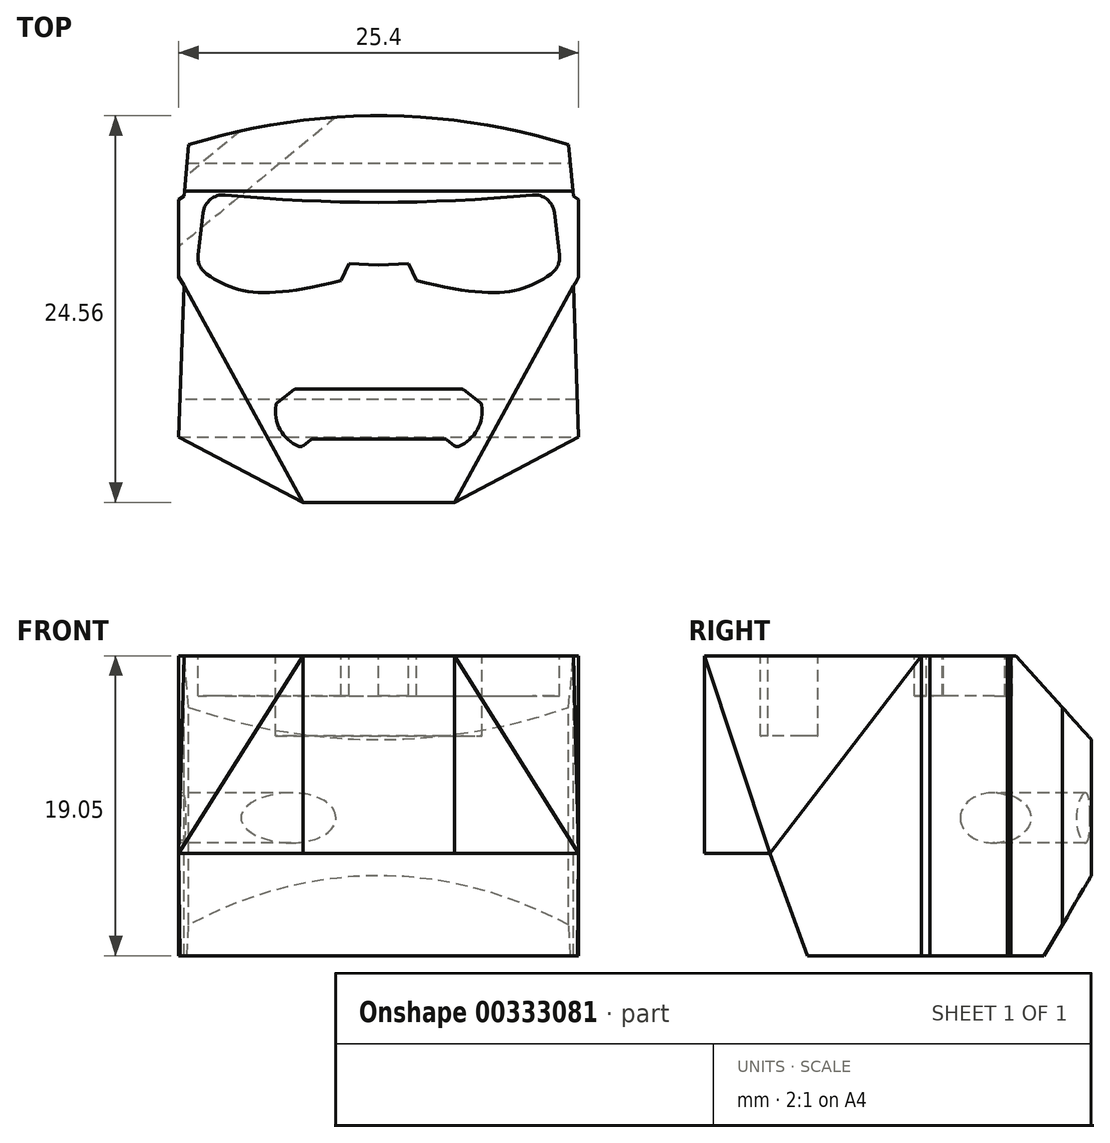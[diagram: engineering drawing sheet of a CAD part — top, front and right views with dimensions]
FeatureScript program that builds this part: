
annotation { "Feature Type Name" : "Feature", "Feature Type Description" : "" }
export const myFeature = defineFeature(function(context is Context, id is Id, definition is map)
    precondition{}
    {
        {
            var Q0;
            Q0=qCreatedBy(makeId("Top.planeOp"),FACE);
            var sketch = newSketch(context, id + "F0", { "sketchPlane" : qUnion([Q0])});
            skLineSegment(sketch, "E0.bottom", {"start": v(-12.7, 12.7) * mm, "end": v(12.7, 12.7) * mm});
            skLineSegment(sketch, "E0.top", {"start": v(-12.7, -12.7) * mm, "end": v(12.7, -12.7) * mm});
            skLineSegment(sketch, "E0.left", {"start": v(-12.7, 12.7) * mm, "end": v(-12.7, -12.7) * mm});
            skLineSegment(sketch, "E0.right", {"start": v(12.7, 12.7) * mm, "end": v(12.7, -12.7) * mm});
            skPoint(sketch, "E0.middle", {"position": v(0, 0) * mm});
            skSolve(sketch);
        }
        {
            var Q0;
            Q0 = qSketchRegion(id + "F0", true);
            extrude(context, id + "F1", {"entities" : qUnion([Q0]), "depth" : 19.05 * mm});
        }
        {
            var Q0;
            Q0=makeQuery(id+"F1.opExtrude","CAP_FACE",FACE,{"disambiguationData":[OSD([sQuery(id+"F0.wireOp",EDGE,"E0.bottom"),sQuery(id+"F0.wireOp",EDGE,"E0.top"),sQuery(id+"F0.wireOp",EDGE,"E0.left"),sQuery(id+"F0.wireOp",EDGE,"E0.right")])],"isStart":false});
            var sketch = newSketch(context, id + "F2", { "sketchPlane" : qUnion([Q0])});
            skLineSegment(sketch, "E1", {"start": v(-12.07, 10.02) * mm, "end": v(12.07, 10.02) * mm, "construction": true});
            skArc(sketch, "E2", {"start": v(12.06, 10.02) * mm, "mid": v(0, 11.86) * mm, "end": v(-12.07, 10.02) * mm});
            skLineSegment(sketch, "E3", {"start": v(-12.07, 10.02) * mm, "end": v(-12.38, 6.75) * mm});
            skLineSegment(sketch, "E4", {"start": v(-12.38, 6.75) * mm, "end": v(-12.7, 6.54) * mm});
            skLineSegment(sketch, "E5", {"start": v(-12.7, 6.54) * mm, "end": v(-12.7, 1.62) * mm});
            skLineSegment(sketch, "E6", {"start": v(-12.7, 1.62) * mm, "end": v(-12.38, 1.07) * mm});
            skLineSegment(sketch, "E7", {"start": v(-12.38, 1.07) * mm, "end": v(-12.7, -8.54) * mm});
            skLineSegment(sketch, "E8", {"start": v(-12.7, -8.54) * mm, "end": v(-4.82, -12.7) * mm});
            skLineSegment(sketch, "E9", {"start": v(-4.82, -12.7) * mm, "end": v(0, -12.7) * mm});
            skLineSegment(sketch, "E10.MirrorCS", {"start": v(4.82, -12.7) * mm, "end": v(0, -12.7) * mm});
            skLineSegment(sketch, "E11.MirrorCS", {"start": v(12.07, 10.02) * mm, "end": v(12.38, 6.75) * mm});
            skLineSegment(sketch, "E12.MirrorCS", {"start": v(12.7, 1.62) * mm, "end": v(12.38, 1.07) * mm});
            skLineSegment(sketch, "E13.MirrorCS", {"start": v(12.38, 6.75) * mm, "end": v(12.7, 6.54) * mm});
            skLineSegment(sketch, "E14.MirrorCS", {"start": v(12.38, 1.07) * mm, "end": v(12.7, -8.54) * mm});
            skLineSegment(sketch, "E15.MirrorCS", {"start": v(12.7, 6.54) * mm, "end": v(12.7, 1.62) * mm});
            skLineSegment(sketch, "E16.MirrorCS", {"start": v(12.7, -8.54) * mm, "end": v(4.82, -12.7) * mm});
            skLineSegment(sketch, "E17.bottom", {"start": v(15.39, 14.33) * mm, "end": v(-17.73, 14.33) * mm});
            skLineSegment(sketch, "E17.top", {"start": v(15.39, -14.33) * mm, "end": v(-17.73, -14.33) * mm});
            skLineSegment(sketch, "E17.left", {"start": v(15.39, 14.33) * mm, "end": v(15.39, -14.33) * mm});
            skLineSegment(sketch, "E17.right", {"start": v(-17.73, 14.33) * mm, "end": v(-17.73, -14.33) * mm});
            skPoint(sketch, "E17.middle", {"position": v(-1.17, 0) * mm});
            skSolve(sketch);
        }
        {
            var Q0;
            Q0 = qSketchRegion(id + "F2", true);
            extrude(context, id + "F3", {"entities" : qUnion([Q0]), "operationType" : NewBodyOperationType.REMOVE, "endBound" : BoundingType.THROUGH_ALL, "oppositeDirection" : true, "depth" : 25.4 * mm});
        }
        {
            var Q0;
            Q0=qCreatedBy(makeId("Right.planeOp"),FACE);
            var sketch = newSketch(context, id + "F4", { "sketchPlane" : qUnion([Q0])});
            skLineSegment(sketch, "E18", {"start": v(6.62, 19.56) * mm, "end": v(12.73, 12.77) * mm});
            skLineSegment(sketch, "E19", {"start": v(12.73, 12.77) * mm, "end": v(13.43, 23.23) * mm});
            skLineSegment(sketch, "E20", {"start": v(13.43, 23.23) * mm, "end": v(6.62, 19.56) * mm});
            skSolve(sketch);
        }
        {
            var Q0;
            Q0 = qSketchRegion(id + "F4", true);
            extrude(context, id + "F5", {"entities" : qUnion([Q0]), "operationType" : NewBodyOperationType.REMOVE, "endBound" : BoundingType.SYMMETRIC, "oppositeDirection" : true, "depth" : 25.4 * mm});
        }
        {
            var Q0;
            Q0=makeQuery(id+"F1.opExtrude","CAP_FACE",FACE,{"disambiguationData":[OSD([sQuery(id+"F0.wireOp",EDGE,"E0.bottom"),sQuery(id+"F0.wireOp",EDGE,"E0.top"),sQuery(id+"F0.wireOp",EDGE,"E0.left"),sQuery(id+"F0.wireOp",EDGE,"E0.right")])],"isStart":false});
            var sketch = newSketch(context, id + "F6", { "sketchPlane" : qUnion([Q0])});
            skLineSegment(sketch, "E21", {"start": v(-12.07, 7.08) * mm, "end": v(12.07, 7.08) * mm, "construction": true});
            skArc(sketch, "E22", {"start": v(-11, 6.95) * mm, "mid": v(0, 6.36) * mm, "end": v(11, 6.95) * mm});
            skLineSegment(sketch, "E23", {"start": v(-11.1, 6.08) * mm, "end": v(-11.56, 2.27) * mm});
            skLineSegment(sketch, "E24", {"start": v(-1.88, 2.47) * mm, "end": v(-2.4, 1.38) * mm});
            skFitSpline(sketch, "E25", {"points": [v(-2.4, 1.38) * mm, v(-11.56, 2.27) * mm, v(-15.68, 7.59) * mm, v(-11.87, 11.56) * mm], "startDerivative": vector(-43.33, -10.8) * mm, "endDerivative": vector(19.12, 12.94) * mm});
            skLineSegment(sketch, "E26.MirrorCS", {"start": v(11.1, 6.08) * mm, "end": v(11.56, 2.27) * mm});
            skLineSegment(sketch, "E27.MirrorCS", {"start": v(1.88, 2.47) * mm, "end": v(2.4, 1.38) * mm});
            skFitSpline(sketch, "E28.MirrorCS", {"points": [v(2.4, 1.38) * mm, v(11.56, 2.27) * mm, v(15.68, 7.59) * mm, v(11.87, 11.56) * mm], "startDerivative": vector(43.33, -10.8) * mm, "endDerivative": vector(-19.12, 12.94) * mm});
            skLineSegment(sketch, "E29.trimOffspring", {"start": v(-1.88, 2.47) * mm, "end": v(0, 2.38) * mm});
            skLineSegment(sketch, "E30.trimOffspring", {"start": v(1.88, 2.47) * mm, "end": v(0, 2.38) * mm});
            skLineSegment(sketch, "E31", {"start": v(-11.1, 6.08) * mm, "end": v(-11, 6.95) * mm});
            skPoint(sketch, "E32.end.orphan", {"position": v(-12.22, 6.13) * mm});
            skLineSegment(sketch, "E33", {"start": v(11.1, 6.08) * mm, "end": v(11, 6.95) * mm});
            skPoint(sketch, "E34.MirrorCS.end.orphan", {"position": v(12.22, 6.13) * mm});
            skPoint(sketch, "E34.MirrorCS.start.orphan", {"position": v(12.06, 7.08) * mm});
            skSolve(sketch);
        }
        {
            var Q0;
            Q0 = qSketchRegion(id + "F6", true);
            extrude(context, id + "F7", {"entities" : qUnion([Q0]), "operationType" : NewBodyOperationType.REMOVE, "oppositeDirection" : true, "depth" : 2.54 * mm});
        }
        {
            var Q0;
            Q0=qCreatedBy(makeId("Right.planeOp"),FACE);
            var sketch = newSketch(context, id + "F8", { "sketchPlane" : qUnion([Q0])});
            skLineSegment(sketch, "E35", {"start": v(12.37, 5.95) * mm, "end": v(7.82, -1.76) * mm});
            skLineSegment(sketch, "E36", {"start": v(7.82, -1.76) * mm, "end": v(16.26, -3) * mm});
            skLineSegment(sketch, "E37", {"start": v(16.26, -3) * mm, "end": v(12.37, 5.95) * mm});
            skLineSegment(sketch, "E38", {"start": v(-5.85, -0.88) * mm, "end": v(-8.54, 6.51) * mm});
            skLineSegment(sketch, "E39", {"start": v(-8.54, 6.51) * mm, "end": v(-13.6, 6.51) * mm});
            skLineSegment(sketch, "E40", {"start": v(-13.6, 6.51) * mm, "end": v(-14.03, -2.36) * mm});
            skLineSegment(sketch, "E41", {"start": v(-14.03, -2.36) * mm, "end": v(-5.85, -0.88) * mm});
            skSolve(sketch);
        }
        {
            var Q0;
            Q0 = qSketchRegion(id + "F8", true);
            extrude(context, id + "F9", {"entities" : qUnion([Q0]), "operationType" : NewBodyOperationType.REMOVE, "endBound" : BoundingType.SYMMETRIC, "oppositeDirection" : true, "depth" : 25.4 * mm});
        }
        {
            var Q0;
            Q0=makeQuery(id+"F3.boolean.opBoolean","COPY",VERTEX,{"derivedFrom":makeQuery(id+"F3.opExtrude","CAP_VERTEX",VERTEX,{"disambiguationData":[OSD([sQuery(id+"F2.wireOp",EDGE,"E12.MirrorCS"),sQuery(id+"F2.wireOp",EDGE,"E14.MirrorCS")])],"isStart":true})});
            var Q1;
            Q1=makeQuery(id+"F3.boolean.opBoolean","COPY",VERTEX,{"derivedFrom":makeQuery(id+"F3.opExtrude","CAP_VERTEX",VERTEX,{"disambiguationData":[OSD([sQuery(id+"F0.wireOp",EDGE,"E0.top"),sQuery(id+"F2.wireOp",EDGE,"E10.MirrorCS"),sQuery(id+"F2.wireOp",EDGE,"E16.MirrorCS")])],"isStart":true})});
            var Q2;
            Q2=makeQuery(id+"F9.boolean.opBoolean","COPY",VERTEX,{"derivedFrom":makeQuery(id+"F9.opExtrude","CAP_VERTEX",VERTEX,{"disambiguationData":[OSD([sQuery(id+"F8.wireOp",EDGE,"E38"),sQuery(id+"F8.wireOp",EDGE,"E39")])],"isStart":true})});
            cPlane(context, id + "F10", {"entities" : qUnion([Q0, Q1, Q2]), "cplaneType" : CPlaneType.THREE_POINT, "offset" : 25.4 * mm, "width" : 152.4 * mm, "height" : 152.4 * mm});
        }
        {
            var Q0;
            Q0=qCreatedBy(id+"F10.planeOp",FACE);
            var sketch = newSketch(context, id + "F11", { "sketchPlane" : qUnion([Q0])});
            skLineSegment(sketch, "E42", {"start": v(10.87, 19.46) * mm, "end": v(-6.75, 22.2) * mm});
            skLineSegment(sketch, "E43", {"start": v(-6.75, 22.2) * mm, "end": v(-12.3, 3.63) * mm});
            skLineSegment(sketch, "E44", {"start": v(-12.3, 3.63) * mm, "end": v(-6.1, -4.82) * mm});
            skLineSegment(sketch, "E45", {"start": v(-6.1, -4.82) * mm, "end": v(9.39, -6.65) * mm});
            skLineSegment(sketch, "E46", {"start": v(9.39, -6.65) * mm, "end": v(10.87, 19.46) * mm});
            skSolve(sketch);
        }
        {
            var Q0;
            Q0 = qSketchRegion(id + "F11", true);
            extrude(context, id + "F12", {"entities" : qUnion([Q0]), "operationType" : NewBodyOperationType.REMOVE, "oppositeDirection" : true, "depth" : 25.4 * mm});
        }
        {
            var Q0;
            Q0=makeQuery(id+"F3.boolean.opBoolean","COPY",VERTEX,{"derivedFrom":makeQuery(id+"F3.opExtrude","CAP_VERTEX",VERTEX,{"disambiguationData":[OSD([sQuery(id+"F2.wireOp",EDGE,"E6"),sQuery(id+"F2.wireOp",EDGE,"E7")])],"isStart":true})});
            var Q1;
            Q1=makeQuery(id+"F3.boolean.opBoolean","COPY",VERTEX,{"derivedFrom":makeQuery(id+"F3.opExtrude","CAP_VERTEX",VERTEX,{"disambiguationData":[OSD([sQuery(id+"F0.wireOp",EDGE,"E0.top"),sQuery(id+"F2.wireOp",EDGE,"E8"),sQuery(id+"F2.wireOp",EDGE,"E9")])],"isStart":true})});
            var Q2;
            Q2=makeQuery(id+"F9.boolean.opBoolean","COPY",VERTEX,{"derivedFrom":makeQuery(id+"F9.opExtrude","CAP_VERTEX",VERTEX,{"disambiguationData":[OSD([sQuery(id+"F8.wireOp",EDGE,"E38"),sQuery(id+"F8.wireOp",EDGE,"E39")])],"isStart":false})});
            cPlane(context, id + "F13", {"entities" : qUnion([Q0, Q1, Q2]), "cplaneType" : CPlaneType.THREE_POINT, "offset" : 25.4 * mm, "width" : 152.4 * mm, "height" : 152.4 * mm});
        }
        {
            var Q0;
            Q0=qCreatedBy(id+"F13.planeOp",FACE);
            var sketch = newSketch(context, id + "F14", { "sketchPlane" : qUnion([Q0])});
            skLineSegment(sketch, "E47", {"start": v(-11.2, 21.08) * mm, "end": v(12.1, 22.2) * mm});
            skLineSegment(sketch, "E48", {"start": v(12.1, 22.2) * mm, "end": v(12.1, -6) * mm});
            skLineSegment(sketch, "E49", {"start": v(12.1, -6) * mm, "end": v(-8.92, -6) * mm});
            skLineSegment(sketch, "E50", {"start": v(-8.92, -6) * mm, "end": v(-11.2, 21.08) * mm});
            skSolve(sketch);
        }
        {
            var Q0;
            Q0 = qSketchRegion(id + "F14", true);
            extrude(context, id + "F15", {"entities" : qUnion([Q0]), "operationType" : NewBodyOperationType.REMOVE, "depth" : 25.4 * mm});
        }
        {
            var Q0;
            Q0=makeQuery(id+"F1.opExtrude","CAP_FACE",FACE,{"disambiguationData":[OSD([sQuery(id+"F0.wireOp",EDGE,"E0.bottom"),sQuery(id+"F0.wireOp",EDGE,"E0.top"),sQuery(id+"F0.wireOp",EDGE,"E0.left"),sQuery(id+"F0.wireOp",EDGE,"E0.right")])],"isStart":false});
            var sketch = newSketch(context, id + "F16", { "sketchPlane" : qUnion([Q0])});
            skLineSegment(sketch, "E51", {"start": v(0, -5.5) * mm, "end": v(-5.3, -5.5) * mm});
            skLineSegment(sketch, "E52", {"start": v(-5.3, -5.5) * mm, "end": v(-6.5, -6.4) * mm});
            skLineSegment(sketch, "E53.0", {"start": v(-4.24, -8.67) * mm, "end": v(-4.92, -9.19) * mm});
            skLineSegment(sketch, "E53.1", {"start": v(0, -8.67) * mm, "end": v(-4.24, -8.67) * mm});
            skArc(sketch, "E54", {"start": v(-6.5, -6.4) * mm, "mid": v(-6.25, -8.1) * mm, "end": v(-4.92, -9.19) * mm});
            skLineSegment(sketch, "E55.MirrorCS", {"start": v(5.3, -5.5) * mm, "end": v(6.5, -6.4) * mm});
            skArc(sketch, "E56.MirrorCS", {"start": v(6.5, -6.4) * mm, "mid": v(6.25, -8.1) * mm, "end": v(4.92, -9.19) * mm});
            skLineSegment(sketch, "E57.MirrorCS", {"start": v(0, -5.5) * mm, "end": v(5.3, -5.5) * mm});
            skLineSegment(sketch, "E58.MirrorCS", {"start": v(0, -8.67) * mm, "end": v(4.24, -8.67) * mm});
            skLineSegment(sketch, "E59.MirrorCS", {"start": v(4.24, -8.67) * mm, "end": v(4.92, -9.19) * mm});
            skSolve(sketch);
        }
        {
            var Q0;
            Q0 = qSketchRegion(id + "F16", true);
            extrude(context, id + "F17", {"entities" : qUnion([Q0]), "operationType" : NewBodyOperationType.REMOVE, "oppositeDirection" : true, "depth" : 5.08 * mm});
        }
        {
            var Q0;
            Q0=makeQuery(id+"F7.boolean.opBoolean","COPY",EDGE,{"derivedFrom":makeQuery(id+"F7.opExtrude","SWEPT_EDGE",EDGE,{"disambiguationData":[OSD([sQuery(id+"F6.wireOp",EDGE,"E22"),sQuery(id+"F6.wireOp",EDGE,"E31")])]})});
            var Q1;
            Q1=makeQuery(id+"F7.boolean.opBoolean","COPY",EDGE,{"derivedFrom":makeQuery(id+"F7.opExtrude","SWEPT_EDGE",EDGE,{"disambiguationData":[OSD([sQuery(id+"F6.wireOp",EDGE,"E22"),sQuery(id+"F6.wireOp",EDGE,"E33")])]})});
            var Q2;
            Q2=makeQuery(id+"F7.boolean.opBoolean","COPY",EDGE,{"derivedFrom":makeQuery(id+"F7.opExtrude","SWEPT_EDGE",EDGE,{"disambiguationData":[OSD([sQuery(id+"F6.wireOp",EDGE,"E26.MirrorCS"),sQuery(id+"F6.wireOp",EDGE,"E28.MirrorCS")])]})});
            var Q3;
            Q3=makeQuery(id+"F7.boolean.opBoolean","COPY",EDGE,{"derivedFrom":makeQuery(id+"F7.opExtrude","SWEPT_EDGE",EDGE,{"disambiguationData":[OSD([sQuery(id+"F6.wireOp",EDGE,"E23"),sQuery(id+"F6.wireOp",EDGE,"E25")])]})});
            fillet(context, id + "F18", {"entities" : qUnion([Q0, Q1, Q2, Q3]), "radius" : 1.27 * mm, "tangentPropagation" : true, "allowEdgeOverflow" : false});
        }
        {
            var Q0;
            Q0=makeQuery(id+"F3.boolean.opBoolean","COPY",FACE,{"derivedFrom":makeQuery(id+"F3.opExtrude","SWEPT_FACE",FACE,{"disambiguationData":[OSD([sQuery(id+"F2.wireOp",EDGE,"E3")])]})});
            var Q1;
            Q1=makeQuery(id+"F3.boolean.opBoolean","COPY",EDGE,{"derivedFrom":makeQuery(id+"F3.opExtrude","SWEPT_EDGE",EDGE,{"disambiguationData":[OSD([sQuery(id+"F2.wireOp",EDGE,"E3"),sQuery(id+"F2.wireOp",EDGE,"E4")])]})});
            cPlane(context, id + "F19", {"entities" : qUnion([Q0, Q1]), "cplaneType" : CPlaneType.LINE_ANGLE, "offset" : 25.4 * mm, "angle" : 45 * degree, "width" : 152.4 * mm, "height" : 152.4 * mm});
        }
        {
            var Q0;
            Q0=qCreatedBy(id+"F19.planeOp",FACE);
            var sketch = newSketch(context, id + "F20", { "sketchPlane" : qUnion([Q0])});
            skCircle(sketch, "E60", {"center": v(12.4, 8.76) * mm, "radius": 1.59 * mm});
            skSolve(sketch);
        }
        {
            var Q0;
            Q0 = qSketchRegion(id + "F20", true);
            extrude(context, id + "F21", {"entities" : qUnion([Q0]), "operationType" : NewBodyOperationType.REMOVE, "endBound" : BoundingType.SYMMETRIC, "depth" : 25.4 * mm});
        }
        {
            var Q0;
            Q0=makeQuery(id+"F17.boolean.opBoolean","COPY",EDGE,{"derivedFrom":makeQuery(id+"F17.opExtrude","SWEPT_EDGE",EDGE,{"disambiguationData":[OSD([sQuery(id+"F16.wireOp",EDGE,"E53.0"),sQuery(id+"F16.wireOp",EDGE,"E53.1")])]})});
            var Q1;
            Q1=makeQuery(id+"F17.boolean.opBoolean","COPY",EDGE,{"derivedFrom":makeQuery(id+"F17.opExtrude","SWEPT_EDGE",EDGE,{"disambiguationData":[OSD([sQuery(id+"F16.wireOp",EDGE,"E53.0"),sQuery(id+"F16.wireOp",EDGE,"E54")])]})});
            var Q2;
            Q2=makeQuery(id+"F17.boolean.opBoolean","COPY",EDGE,{"derivedFrom":makeQuery(id+"F17.opExtrude","SWEPT_EDGE",EDGE,{"disambiguationData":[OSD([sQuery(id+"F16.wireOp",EDGE,"E52"),sQuery(id+"F16.wireOp",EDGE,"E54")])]})});
            var Q3;
            Q3=makeQuery(id+"F17.boolean.opBoolean","COPY",EDGE,{"derivedFrom":makeQuery(id+"F17.opExtrude","SWEPT_EDGE",EDGE,{"disambiguationData":[OSD([sQuery(id+"F16.wireOp",EDGE,"E51"),sQuery(id+"F16.wireOp",EDGE,"E52")])]})});
            var Q4;
            Q4=makeQuery(id+"F17.boolean.opBoolean","COPY",EDGE,{"derivedFrom":makeQuery(id+"F17.opExtrude","SWEPT_EDGE",EDGE,{"disambiguationData":[OSD([sQuery(id+"F16.wireOp",EDGE,"E58.MirrorCS"),sQuery(id+"F16.wireOp",EDGE,"E59.MirrorCS")])]})});
            var Q5;
            Q5=makeQuery(id+"F17.boolean.opBoolean","COPY",EDGE,{"derivedFrom":makeQuery(id+"F17.opExtrude","SWEPT_EDGE",EDGE,{"disambiguationData":[OSD([sQuery(id+"F16.wireOp",EDGE,"E56.MirrorCS"),sQuery(id+"F16.wireOp",EDGE,"E59.MirrorCS")])]})});
            var Q6;
            Q6=makeQuery(id+"F17.boolean.opBoolean","COPY",EDGE,{"derivedFrom":makeQuery(id+"F17.opExtrude","SWEPT_EDGE",EDGE,{"disambiguationData":[OSD([sQuery(id+"F16.wireOp",EDGE,"E55.MirrorCS"),sQuery(id+"F16.wireOp",EDGE,"E56.MirrorCS")])]})});
            var Q7;
            Q7=makeQuery(id+"F17.boolean.opBoolean","COPY",EDGE,{"derivedFrom":makeQuery(id+"F17.opExtrude","SWEPT_EDGE",EDGE,{"disambiguationData":[OSD([sQuery(id+"F16.wireOp",EDGE,"E55.MirrorCS"),sQuery(id+"F16.wireOp",EDGE,"E57.MirrorCS")])]})});
            fillet(context, id + "F22", {"entities" : qUnion([Q0, Q1, Q2, Q3, Q4, Q5, Q6, Q7]), "radius" : 0.25 * mm, "tangentPropagation" : true, "allowEdgeOverflow" : false});
        }
    });
